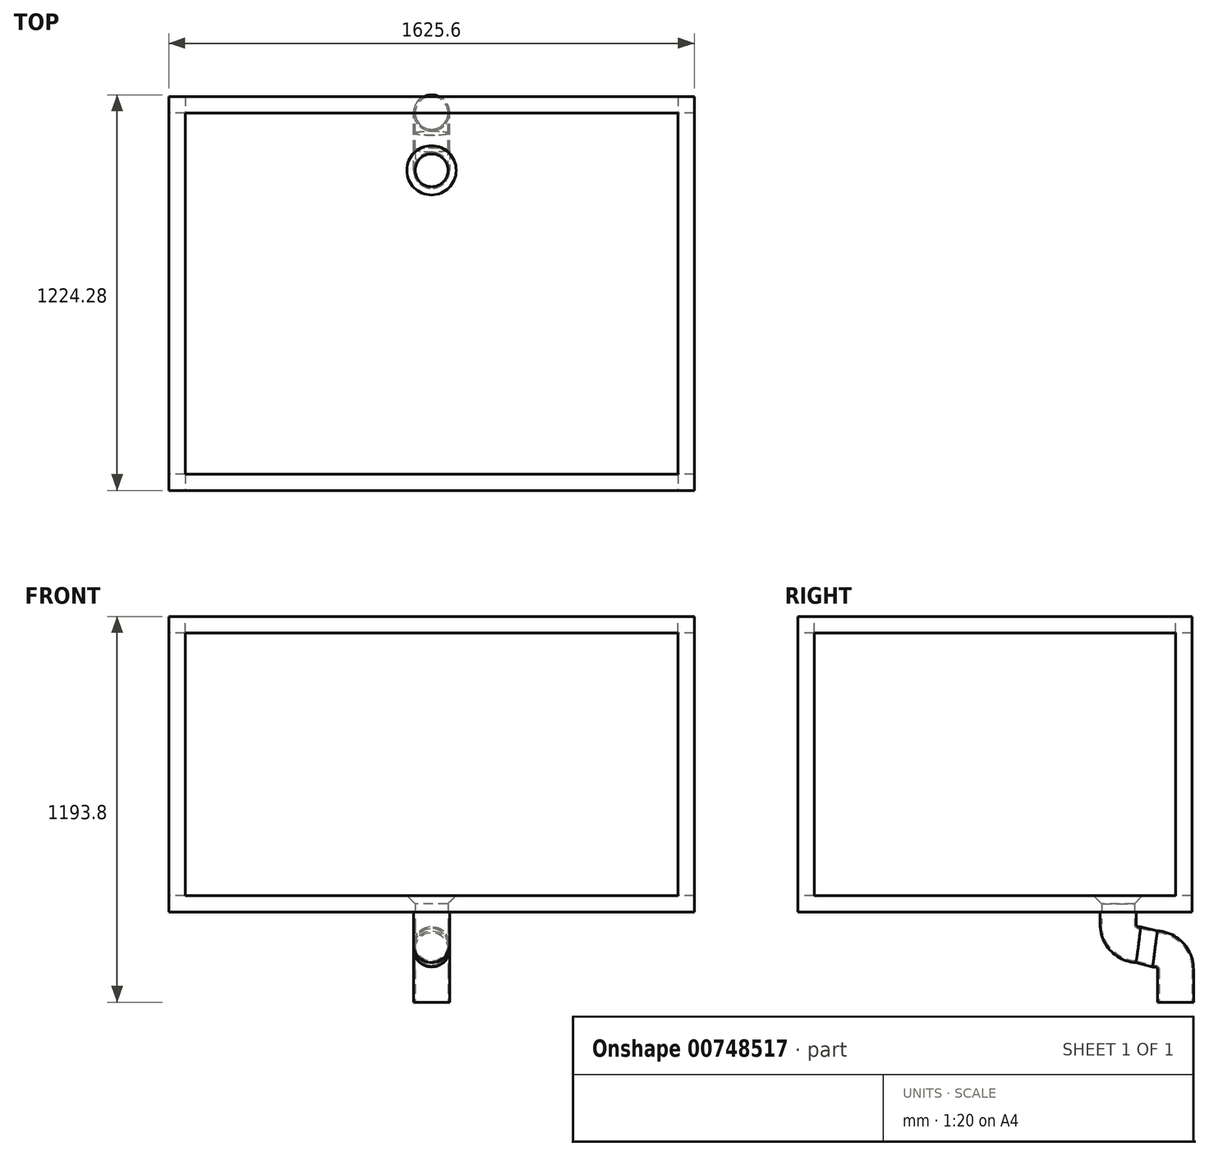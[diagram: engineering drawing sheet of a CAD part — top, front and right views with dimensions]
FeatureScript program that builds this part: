
annotation { "Feature Type Name" : "Feature", "Feature Type Description" : "" }
export const myFeature = defineFeature(function(context is Context, id is Id, definition is map)
    precondition{}
    {
        {
            var Q0;
            Q0=qCreatedBy(makeId("Top.planeOp"),FACE);
            var sketch = newSketch(context, id + "F0", { "sketchPlane" : qUnion([Q0])});
            skLineSegment(sketch, "E0.bottom", {"start": v(609.6, -508) * mm, "end": v(-609.6, -508) * mm, "construction": true});
            skLineSegment(sketch, "E0.top", {"start": v(609.6, 508) * mm, "end": v(-609.6, 508) * mm, "construction": true});
            skLineSegment(sketch, "E0.left", {"start": v(609.6, -508) * mm, "end": v(609.6, 508) * mm, "construction": true});
            skLineSegment(sketch, "E0.right", {"start": v(-609.6, -508) * mm, "end": v(-609.6, 508) * mm, "construction": true});
            skPoint(sketch, "E0.middle", {"position": v(0, 0) * mm});
            skLineSegment(sketch, "E1.bottom", {"start": v(812.8, 609.6) * mm, "end": v(-812.8, 609.6) * mm});
            skLineSegment(sketch, "E1.top", {"start": v(812.8, -609.6) * mm, "end": v(-812.8, -609.6) * mm});
            skLineSegment(sketch, "E1.left", {"start": v(812.8, 609.6) * mm, "end": v(812.8, -609.6) * mm});
            skLineSegment(sketch, "E1.right", {"start": v(-812.8, 609.6) * mm, "end": v(-812.8, -609.6) * mm});
            skLineSegment(sketch, "E2", {"start": v(0, 0) * mm, "end": v(0, 381) * mm, "construction": true});
            skCircle(sketch, "E3", {"center": v(0, 381) * mm, "radius": 50.8 * mm});
            skSolve(sketch);
        }
        {
            var Q0;
            Q0 = qSketchRegion(id + "F0", true);
            extrude(context, id + "F1", {"entities" : qUnion([Q0]), "depth" : 914.4 * mm, "offsetDistance" : 25.4 * mm});
        }
        {
            var Q0;
            Q0=makeQuery(id+"F1.opExtrude","CAP_FACE",FACE,{"disambiguationData":[OSD([sQuery(id+"F0.wireOp",EDGE,"E1.bottom"),sQuery(id+"F0.wireOp",EDGE,"E1.top"),sQuery(id+"F0.wireOp",EDGE,"E1.left"),sQuery(id+"F0.wireOp",EDGE,"E1.right"),sQuery(id+"F0.wireOp",EDGE,"E3")])],"isStart":false});
            var sketch = newSketch(context, id + "F2", { "sketchPlane" : qUnion([Q0])});
            skLineSegment(sketch, "E4.0", {"start": v(-762, 558.8) * mm, "end": v(-762, -558.8) * mm});
            skLineSegment(sketch, "E4.1", {"start": v(762, 558.8) * mm, "end": v(-762, 558.8) * mm});
            skLineSegment(sketch, "E4.2", {"start": v(762, 558.8) * mm, "end": v(762, -558.8) * mm});
            skLineSegment(sketch, "E4.3", {"start": v(762, -558.8) * mm, "end": v(-762, -558.8) * mm});
            skSolve(sketch);
        }
        {
            var Q0;
            Q0 = qSketchRegion(id + "F2", true);
            extrude(context, id + "F3", {"entities" : qUnion([Q0]), "operationType" : NewBodyOperationType.REMOVE, "oppositeDirection" : true, "depth" : 863.6 * mm, "offsetDistance" : 25.4 * mm});
        }
        {
            var Q0;
            Q0=makeQuery(id+"F1.opExtrude","SWEPT_FACE",FACE,{"disambiguationData":[OSD([sQuery(id+"F0.wireOp",EDGE,"E1.top")])]});
            var sketch = newSketch(context, id + "F4", { "sketchPlane" : qUnion([Q0])});
            skLineSegment(sketch, "E5.0", {"start": v(-762, 863.6) * mm, "end": v(-762, 50.8) * mm});
            skLineSegment(sketch, "E5.1", {"start": v(762, 863.6) * mm, "end": v(-762, 863.6) * mm});
            skLineSegment(sketch, "E5.2", {"start": v(762, 863.6) * mm, "end": v(762, 50.8) * mm});
            skLineSegment(sketch, "E5.3", {"start": v(762, 50.8) * mm, "end": v(-762, 50.8) * mm});
            skSolve(sketch);
        }
        {
            var Q0;
            Q0 = qSketchRegion(id + "F4", true);
            extrude(context, id + "F5", {"entities" : qUnion([Q0]), "operationType" : NewBodyOperationType.REMOVE, "endBound" : BoundingType.THROUGH_ALL, "oppositeDirection" : true, "depth" : 25.4 * mm, "offsetDistance" : 25.4 * mm});
        }
        {
            var Q0;
            Q0=makeQuery(id+"F1.opExtrude","SWEPT_FACE",FACE,{"disambiguationData":[OSD([sQuery(id+"F0.wireOp",EDGE,"E1.right")])]});
            var sketch = newSketch(context, id + "F6", { "sketchPlane" : qUnion([Q0])});
            skLineSegment(sketch, "E6.0", {"start": v(-558.8, 863.6) * mm, "end": v(-558.8, 50.8) * mm});
            skLineSegment(sketch, "E6.1", {"start": v(-558.8, 863.6) * mm, "end": v(558.8, 863.6) * mm});
            skLineSegment(sketch, "E6.2", {"start": v(558.8, 863.6) * mm, "end": v(558.8, 50.8) * mm});
            skLineSegment(sketch, "E6.3", {"start": v(-558.8, 50.8) * mm, "end": v(558.8, 50.8) * mm});
            skSolve(sketch);
        }
        {
            var Q0;
            Q0 = qSketchRegion(id + "F6", true);
            extrude(context, id + "F7", {"entities" : qUnion([Q0]), "operationType" : NewBodyOperationType.REMOVE, "endBound" : BoundingType.THROUGH_ALL, "oppositeDirection" : true, "depth" : 25.4 * mm, "offsetDistance" : 25.4 * mm});
        }
        {
            var Q0;
            Q0=makeQuery(id+"F3.boolean.opBoolean","INTERSECT",EDGE,{"derivedFrom":[makeQuery(id+"F1.opExtrude","SWEPT_FACE",FACE,{"disambiguationData":[OSD([sQuery(id+"F0.wireOp",EDGE,"E3")])]}),makeQuery(id+"F3.opExtrude","CAP_FACE",FACE,{"disambiguationData":[OSD([sQuery(id+"F2.wireOp",EDGE,"E4.0"),sQuery(id+"F2.wireOp",EDGE,"E4.1"),sQuery(id+"F2.wireOp",EDGE,"E4.2"),sQuery(id+"F2.wireOp",EDGE,"E4.3")])],"isStart":false})]});
            chamfer(context, id + "F8", {"entities" : qUnion([Q0]), "width" : 25.4 * mm, "tangentPropagation" : true});
        }
        {
            var Q0;
            Q0=qCreatedBy(makeId("Right.planeOp"),FACE);
            var sketch = newSketch(context, id + "F9", { "sketchPlane" : qUnion([Q0])});
            skLineSegment(sketch, "E7", {"start": v(381, 0) * mm, "end": v(381, -38.1) * mm});
            skLineSegment(sketch, "E8", {"start": v(381, -38.1) * mm, "end": v(444.5, -38.1) * mm, "construction": true});
            skLineSegment(sketch, "E9", {"start": v(444.5, -38.1) * mm, "end": v(444.5, -101.6) * mm, "construction": true});
            skLineSegment(sketch, "E10", {"start": v(444.5, -101.6) * mm, "end": v(495.3, -101.6) * mm, "construction": true});
            skLineSegment(sketch, "E11", {"start": v(495.3, -101.6) * mm, "end": v(495.3, -114.3) * mm, "construction": true});
            skLineSegment(sketch, "E12", {"start": v(495.3, -114.3) * mm, "end": v(444.5, -101.6) * mm});
            skLineSegment(sketch, "E13", {"start": v(495.3, -114.3) * mm, "end": v(495.3, -177.8) * mm, "construction": true});
            skLineSegment(sketch, "E14", {"start": v(495.3, -177.8) * mm, "end": v(558.8, -177.8) * mm, "construction": true});
            skLineSegment(sketch, "E15", {"start": v(558.8, -177.8) * mm, "end": v(558.8, -279.4) * mm});
            skCircle(sketch, "E16", {"center": v(444.5, -38.1) * mm, "radius": 63.5 * mm, "construction": true});
            skCircle(sketch, "E17", {"center": v(495.3, -177.8) * mm, "radius": 63.5 * mm, "construction": true});
            skArc(sketch, "E18", {"start": v(381, -38.1) * mm, "mid": v(399.6, -83) * mm, "end": v(444.5, -101.6) * mm});
            skArc(sketch, "E19", {"start": v(558.8, -177.8) * mm, "mid": v(540.2, -132.9) * mm, "end": v(495.3, -114.3) * mm});
            skSolve(sketch);
        }
        {
            var Q0;
            Q0=makeQuery(id+"F1.opExtrude","CAP_FACE",FACE,{"disambiguationData":[OSD([sQuery(id+"F0.wireOp",EDGE,"E1.bottom"),sQuery(id+"F0.wireOp",EDGE,"E1.top"),sQuery(id+"F0.wireOp",EDGE,"E1.left"),sQuery(id+"F0.wireOp",EDGE,"E1.right"),sQuery(id+"F0.wireOp",EDGE,"E3")])],"isStart":true});
            var sketch = newSketch(context, id + "F10", { "sketchPlane" : qUnion([Q0])});
            skCircle(sketch, "E20", {"center": v(0, -381) * mm, "radius": 55.88 * mm});
            skCircle(sketch, "E21", {"center": v(0, -381) * mm, "radius": 50.8 * mm});
            skSolve(sketch);
        }
        {
            var Q0;
            Q0 = qSketchRegion(id + "F10", true);
            var Q1;
            Q1 = qConstructionFilter(qBodyType(qCreatedBy(id + "F9" ,EDGE), BodyType.WIRE), ConstructionObject.NO);
            sweep(context, id + "F11", {"operationType" : NewBodyOperationType.ADD, "profiles" : qUnion([Q0]), "path" : qUnion([Q1])});
        }
    });
